# Revit family: Шкаф медицинский навесной двухдверный ДМ-2-002-04
name_source: partatom
category: Оборудование
revit_build: Autodesk Revit 2017 (Build: 20170419_0315(x64)
units: mm (PartAtom-declared; Revit-internal decimal feet)

## family parameters
Всегда вертикально = Да
На основе рабочей плоскости = Нет
Общий = Нет
При загрузке вырезать с полостями = Нет
Размер круглого соединителя = Использовать диаметр
Тип детали = Нормальный
Точка расчета площади = Нет

## types (1)
- Тип
    Длина ручек = 150 мм
    Каркас = Алюминий 7075
    Ножки = Пластмасса, непрозрачная, черная
    Общ_Высота = 450 мм
    Общ_Глубина = 400 мм
    Общ_Единицы измерения = шт.
    Общ_Наименование = Шкаф медицинский навесной двухдверный
    Общ_Поставщик = Доктор Мебель
    Общ_Тип, марка = ДМ-2-002-04
    Общ_Ширина = 900 мм
    Панели = Пластмасса, непрозрачная, белая
    Ручки = Алюминий 7075
    Фасад = Столешница медицинской мебели ДСП с пластиковым покрытием

## geometry (parser evidence)
native form markers: Blend x2
no freeform markers — native parametric forms only
